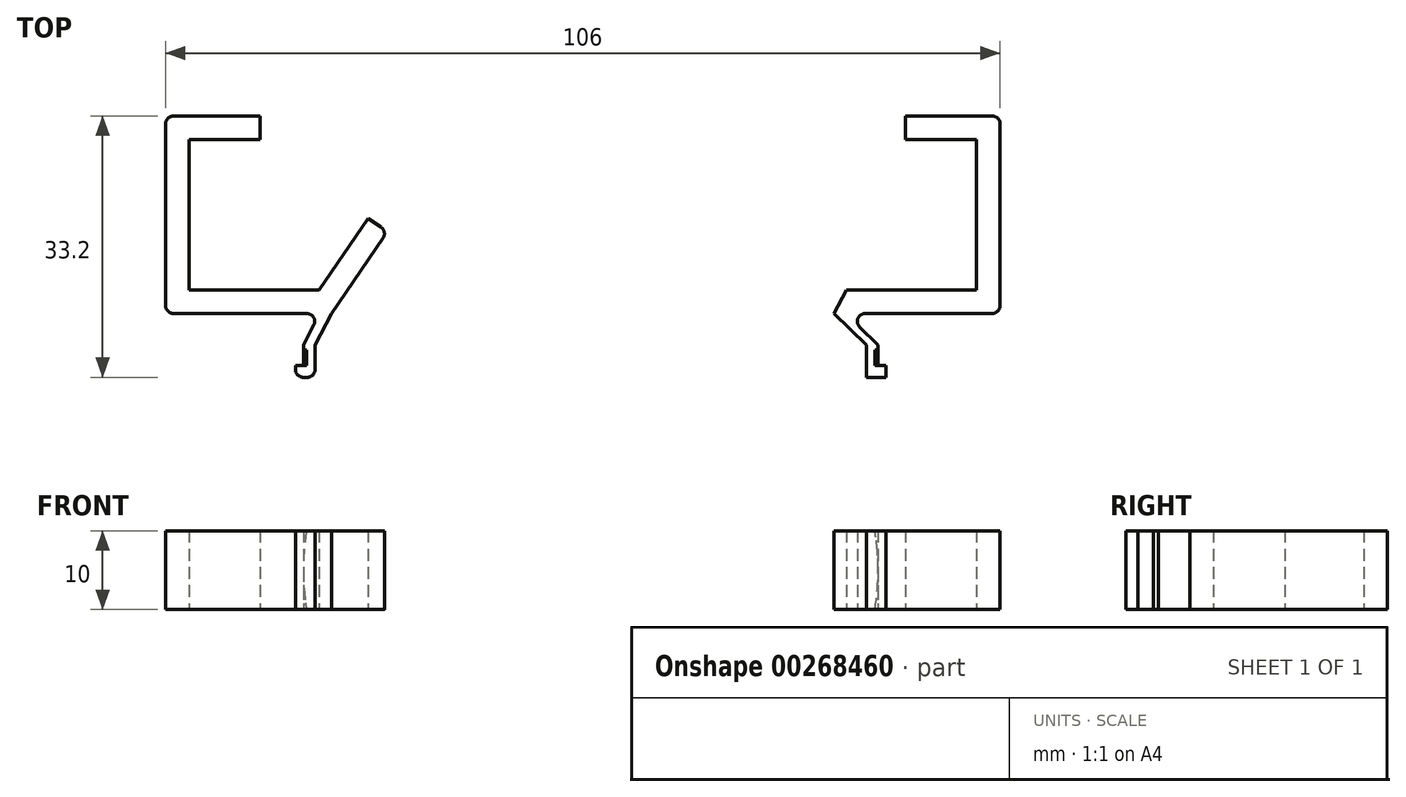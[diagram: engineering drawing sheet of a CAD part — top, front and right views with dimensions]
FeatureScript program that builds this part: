
annotation { "Feature Type Name" : "Feature", "Feature Type Description" : "" }
export const myFeature = defineFeature(function(context is Context, id is Id, definition is map)
    precondition{}
    {
        {
            var Q0;
            Q0=qCreatedBy(makeId("Top.planeOp"),FACE);
            var sketch = newSketch(context, id + "F0", { "sketchPlane" : qUnion([Q0])});
            skLineSegment(sketch, "E0", {"start": v(0, 0) * mm, "end": v(0, 19.1) * mm});
            skLineSegment(sketch, "E1", {"start": v(0, 19.1) * mm, "end": v(9, 19.1) * mm});
            skLineSegment(sketch, "E2", {"start": v(0, 0) * mm, "end": v(16.5, 0) * mm});
            skLineSegment(sketch, "E3", {"start": v(16.5, 0) * mm, "end": v(22.7, 9.1) * mm});
            skLineSegment(sketch, "E4.0", {"start": v(-3, 22.1) * mm, "end": v(9, 22.1) * mm});
            skLineSegment(sketch, "E4.1", {"start": v(-3, -3) * mm, "end": v(-3, 22.1) * mm});
            skLineSegment(sketch, "E4.2", {"start": v(-3, -3) * mm, "end": v(18.09, -3) * mm});
            skLineSegment(sketch, "E4.3", {"start": v(18.09, -3) * mm, "end": v(25.18, 7.41) * mm});
            skLineSegment(sketch, "E5", {"start": v(9, 22.1) * mm, "end": v(9, 19.1) * mm});
            skLineSegment(sketch, "E6", {"start": v(22.7, 9.1) * mm, "end": v(25.18, 7.41) * mm});
            skLineSegment(sketch, "E7", {"start": v(50, 52.55) * mm, "end": v(50, -36.88) * mm, "construction": true});
            skLineSegment(sketch, "E8.MirrorCS", {"start": v(91, 22.1) * mm, "end": v(91, 19.1) * mm});
            skLineSegment(sketch, "E9.MirrorCS", {"start": v(103, -3) * mm, "end": v(103, 22.1) * mm});
            skLineSegment(sketch, "E10.MirrorCS", {"start": v(103, 22.1) * mm, "end": v(91, 22.1) * mm});
            skLineSegment(sketch, "E11.MirrorCS", {"start": v(100, 19.1) * mm, "end": v(91, 19.1) * mm});
            skLineSegment(sketch, "E12.MirrorCS", {"start": v(103, -3) * mm, "end": v(81.91, -3) * mm});
            skLineSegment(sketch, "E13.MirrorCS", {"start": v(100, 0) * mm, "end": v(83.5, 0) * mm});
            skLineSegment(sketch, "E14.MirrorCS", {"start": v(100, 0) * mm, "end": v(100, 19.1) * mm});
            skLineSegment(sketch, "E15.bottom", {"start": v(10.1, -7) * mm, "end": v(14.5, -7) * mm, "construction": true});
            skLineSegment(sketch, "E15.top", {"start": v(10.1, -9.6) * mm, "end": v(14.5, -9.6) * mm});
            skLineSegment(sketch, "E15.left", {"start": v(10.1, -7) * mm, "end": v(10.1, -9.6) * mm, "construction": true});
            skLineSegment(sketch, "E15.right", {"start": v(14.5, -7) * mm, "end": v(14.5, -9.6) * mm});
            skLineSegment(sketch, "E16.0", {"start": v(13.5, -11.1) * mm, "end": v(16, -11.1) * mm});
            skLineSegment(sketch, "E16.1", {"start": v(16, -7) * mm, "end": v(16, -11.1) * mm});
            skLineSegment(sketch, "E17", {"start": v(13.5, -9.6) * mm, "end": v(13.5, -11.1) * mm});
            skLineSegment(sketch, "E18", {"start": v(81.91, -3) * mm, "end": v(86, -7) * mm});
            skLineSegment(sketch, "E19", {"start": v(87.5, -7) * mm, "end": v(83.41, -3) * mm});
            skLineSegment(sketch, "E20", {"start": v(81.91, -3) * mm, "end": v(83.5, 0) * mm});
            skLineSegment(sketch, "E21", {"start": v(87.5, -7) * mm, "end": v(87.5, -9.6) * mm});
            skLineSegment(sketch, "E22", {"start": v(87.5, -9.6) * mm, "end": v(88.5, -9.6) * mm});
            skLineSegment(sketch, "E23", {"start": v(88.5, -9.6) * mm, "end": v(88.5, -11.1) * mm});
            skLineSegment(sketch, "E24", {"start": v(88.5, -11.1) * mm, "end": v(86, -11.1) * mm});
            skLineSegment(sketch, "E25", {"start": v(86, -11.1) * mm, "end": v(86, -7) * mm});
            skLineSegment(sketch, "E26", {"start": v(14.5, -7) * mm, "end": v(16.59, -3) * mm});
            skLineSegment(sketch, "E27", {"start": v(16, -7) * mm, "end": v(18.09, -3) * mm});
            skSolve(sketch);
        }
        {
            var Q0;
            Q0=makeQuery(id+"F0.imprint","IMPRINT",FACE,{"disambiguationData":[TD([[makeQuery(id+"F0.imprint","IMPRINT",EDGE,{"derivedFrom":sQuery(id+"F0.wireOp",EDGE,"E8.MirrorCS")}),1.0]])]});
            var Q1;
            {var subQ2=sQuery(id+"F0.wireOp",EDGE,"7fd3f9bc-cb2d-437e-a477-eb83bc3e467c0.MirrorCS");Q1=makeQuery(id+"F0.imprint","IMPRINT",FACE,{"disambiguationData":[TD([[makeQuery(id+"F0.imprint","IMPRINT",EDGE,{"derivedFrom":subQ2}),1.0]])]});}
            var Q2;
            Q2=makeQuery(id+"F0.imprint","IMPRINT",FACE,{"disambiguationData":[TD([[makeQuery(id+"F0.imprint","IMPRINT",EDGE,{"derivedFrom":sQuery(id+"F0.wireOp",EDGE,"E0")}),1.0]])]});
            var Q3;
            {var subQ1=sQuery(id+"F0.wireOp",EDGE,"E15.right");Q3=makeQuery(id+"F0.imprint","IMPRINT",FACE,{"disambiguationData":[TD([[makeQuery(id+"F0.imprint","IMPRINT",EDGE,{"derivedFrom":subQ1}),1.0]])]});}
            var Q4;
            {var subQ0=sQuery(id+"F0.wireOp",EDGE,"E18");Q4=makeQuery(id+"F0.imprint","IMPRINT",FACE,{"disambiguationData":[TD([[makeQuery(id+"F0.imprint","IMPRINT",EDGE,{"derivedFrom":subQ0}),1.0]])]});}
            extrude(context, id + "F1", {"entities" : qUnion([Q0, Q1, Q2, Q3, Q4]), "depth" : 10 * mm, "offsetDistance" : 25 * mm, "symmetric" : true});
        }
        {
            var Q0;
            Q0=makeQuery(id+"F1.opExtrude","SWEPT_FACE",FACE,{"disambiguationData":[OSD([sQuery(id+"F0.wireOp",EDGE,"E15.top")])]});
            var sketch = newSketch(context, id + "F2", { "sketchPlane" : qUnion([Q0])});
            skPoint(sketch, "E28.0", {"position": v(-87.5, 0) * mm});
            skPoint(sketch, "E29.0", {"position": v(-14.5, 0) * mm});
            skLineSegment(sketch, "E30", {"start": v(-87.5, 0) * mm, "end": v(-14.5, 0) * mm, "construction": true});
            skLineSegment(sketch, "E31", {"start": v(-51, 0) * mm, "end": v(-51, 14.66) * mm, "construction": true});
            skCircle(sketch, "E32", {"center": v(-51, 0) * mm, "radius": 36.5 * mm});
            skCircle(sketch, "E33", {"center": v(-51, 0) * mm, "radius": 39.5 * mm});
            skSolve(sketch);
        }
        {
            var Q0;
            Q0=makeQuery(id+"F1.opExtrude","SWEPT_EDGE",EDGE,{"disambiguationData":[OSD([sQuery(id+"F0.wireOp",EDGE,"E9.MirrorCS"),sQuery(id+"F0.wireOp",EDGE,"E10.MirrorCS")])]});
            var Q1;
            Q1=makeQuery(id+"F1.opExtrude","SWEPT_EDGE",EDGE,{"disambiguationData":[OSD([sQuery(id+"F0.wireOp",EDGE,"E9.MirrorCS"),sQuery(id+"F0.wireOp",EDGE,"E12.MirrorCS")])]});
            var Q2;
            Q2=makeQuery(id+"F1.opExtrude","SWEPT_EDGE",EDGE,{"disambiguationData":[OSD([sQuery(id+"F0.wireOp",EDGE,"5a6db4d1-ee95-410c-8e2b-245da783c4610.MirrorCS"),sQuery(id+"F0.wireOp",EDGE,"12efcd92-a749-4238-9ad8-4c92c0031cb60.MirrorCS")])]});
            var Q3;
            Q3=makeQuery(id+"F1.opExtrude","SWEPT_EDGE",EDGE,{"disambiguationData":[OSD([sQuery(id+"F0.wireOp",EDGE,"12efcd92-a749-4238-9ad8-4c92c0031cb60.MirrorCS"),sQuery(id+"F0.wireOp",EDGE,"af5a5f1a-a19b-42ac-9b84-1e42bc72fd6b0.MirrorCS")])]});
            var Q4;
            Q4=makeQuery(id+"F1.opExtrude","SWEPT_EDGE",EDGE,{"disambiguationData":[OSD([sQuery(id+"F0.wireOp",EDGE,"fc325f98-27ae-4ef3-95bf-a05a649279151.MirrorCS"),sQuery(id+"F0.wireOp",EDGE,"fc325f98-27ae-4ef3-95bf-a05a649279157.MirrorCS")])]});
            var Q5;
            Q5=makeQuery(id+"F1.opExtrude","SWEPT_EDGE",EDGE,{"disambiguationData":[OSD([sQuery(id+"F0.wireOp",EDGE,"E16.0"),sQuery(id+"F0.wireOp",EDGE,"E17")])]});
            var Q6;
            Q6=makeQuery(id+"F1.opExtrude","SWEPT_EDGE",EDGE,{"disambiguationData":[OSD([sQuery(id+"F0.wireOp",EDGE,"E16.0"),sQuery(id+"F0.wireOp",EDGE,"E16.1")])]});
            var Q7;
            Q7=makeQuery(id+"F1.opExtrude","SWEPT_EDGE",EDGE,{"disambiguationData":[OSD([sQuery(id+"F0.wireOp",EDGE,"E4.3"),sQuery(id+"F0.wireOp",EDGE,"E6")])]});
            var Q8;
            Q8=makeQuery(id+"F1.opExtrude","SWEPT_EDGE",EDGE,{"disambiguationData":[OSD([sQuery(id+"F0.wireOp",EDGE,"E4.1"),sQuery(id+"F0.wireOp",EDGE,"E4.2")])]});
            var Q9;
            Q9=makeQuery(id+"F1.opExtrude","SWEPT_EDGE",EDGE,{"disambiguationData":[OSD([sQuery(id+"F0.wireOp",EDGE,"E4.0"),sQuery(id+"F0.wireOp",EDGE,"E4.1")])]});
            fillet(context, id + "F3", {"entities" : qUnion([Q0, Q1, Q2, Q3, Q4, Q5, Q6, Q7, Q8, Q9]), "radius" : 1 * mm, "tangentPropagation" : true, "allowEdgeOverflow" : false});
        }
        {
            var Q0;
            Q0=makeQuery(id+"F1.opExtrude","SWEPT_EDGE",EDGE,{"disambiguationData":[OSD([sQuery(id+"F0.wireOp",EDGE,"E12.MirrorCS"),sQuery(id+"F0.wireOp",EDGE,"E19")])]});
            var Q1;
            Q1=makeQuery(id+"F1.opExtrude","SWEPT_EDGE",EDGE,{"disambiguationData":[OSD([sQuery(id+"F0.wireOp",EDGE,"E4.2"),sQuery(id+"F0.wireOp",EDGE,"E26")])]});
            fillet(context, id + "F4", {"entities" : qUnion([Q0, Q1]), "tangentPropagation" : true, "radius" : 1 * mm, "defaultsChanged" : false, "vertexSettings" : [], "allowEdgeOverflow" : false});
        }
        {
            var Q0;
            {var subQ0=sQuery(id+"F0.wireOp",EDGE,"E15.top");var subQ1=makeQuery(id+"F1.opExtrude","CAP_EDGE",EDGE,{"disambiguationData":[OSD([subQ0])],"isStart":true});Q0=makeQuery(id+"F2.imprint","IMPRINT",FACE,{"disambiguationData":[TD([[makeQuery(id+"F2.imprint","IMPRINT",EDGE,{"derivedFrom":subQ1}),-1.0]])]});}
            var sketch = newSketch(context, id + "F5", { "sketchPlane" : qUnion([Q0])});
            skPoint(sketch, "E34.0", {"position": v(-14.5, 0) * mm});
            skPoint(sketch, "E35.0", {"position": v(-14.5, 5) * mm});
            skPoint(sketch, "E36.0", {"position": v(-14.5, -5) * mm});
            skArc(sketch, "E37", {"start": v(-14.9, -5) * mm, "mid": v(-14.5, 0) * mm, "end": v(-14.9, 5) * mm});
            skLineSegment(sketch, "E38", {"start": v(-14.9, -5) * mm, "end": v(-14.5, -5) * mm});
            skLineSegment(sketch, "E39", {"start": v(-14.5, 0) * mm, "end": v(-14.5, -5) * mm});
            skLineSegment(sketch, "E40", {"start": v(-14.5, 0) * mm, "end": v(-14.5, 5) * mm});
            skLineSegment(sketch, "E41", {"start": v(-14.5, 5) * mm, "end": v(-14.9, 5) * mm});
            skSolve(sketch);
        }
        {
            var Q0;
            {var subQ0=sQuery(id+"F5.wireOp",EDGE,"E40");Q0=makeQuery(id+"F5.imprint","IMPRINT",FACE,{"disambiguationData":[TD([[makeQuery(id+"F5.imprint","IMPRINT",EDGE,{"derivedFrom":subQ0}),-1.0]])]});}
            var Q1;
            {var subQ2=sQuery(id+"F5.wireOp",EDGE,"E38");Q1=makeQuery(id+"F5.imprint","IMPRINT",FACE,{"disambiguationData":[TD([[makeQuery(id+"F5.imprint","IMPRINT",EDGE,{"derivedFrom":subQ2}),1.0]])]});}
            extrude(context, id + "F6", {"entities" : qUnion([Q0, Q1]), "operationType" : NewBodyOperationType.REMOVE, "depth" : 2 * mm, "offsetDistance" : 25 * mm});
        }
        {
            var Q0;
            Q0=makeQuery(id+"F1.opExtrude","SWEPT_FACE",FACE,{"disambiguationData":[OSD([sQuery(id+"F0.wireOp",EDGE,"E22")])]});
            var sketch = newSketch(context, id + "F7", { "sketchPlane" : qUnion([Q0])});
            skPoint(sketch, "E42.0", {"position": v(-87.5, 0) * mm});
            skPoint(sketch, "E43.0", {"position": v(-87.5, 5) * mm});
            skPoint(sketch, "E44.0", {"position": v(-87.5, -5) * mm});
            skArc(sketch, "E45", {"start": v(-87.1, 5) * mm, "mid": v(-87.5, 0) * mm, "end": v(-87.1, -5) * mm});
            skLineSegment(sketch, "E46", {"start": v(-87.1, 5) * mm, "end": v(-87.5, 5) * mm});
            skLineSegment(sketch, "E47", {"start": v(-87.5, 0) * mm, "end": v(-87.5, 5) * mm});
            skLineSegment(sketch, "E48", {"start": v(-87.5, 0) * mm, "end": v(-87.5, -5) * mm});
            skLineSegment(sketch, "E49", {"start": v(-87.5, -5) * mm, "end": v(-87.1, -5) * mm});
            skSolve(sketch);
        }
        {
            var Q0;
            {var subQ0=sQuery(id+"F7.wireOp",EDGE,"E46");Q0=makeQuery(id+"F7.imprint","IMPRINT",FACE,{"disambiguationData":[TD([[makeQuery(id+"F7.imprint","IMPRINT",EDGE,{"derivedFrom":subQ0}),1.0]])]});}
            var Q1;
            {var subQ2=sQuery(id+"F7.wireOp",EDGE,"E48");Q1=makeQuery(id+"F7.imprint","IMPRINT",FACE,{"disambiguationData":[TD([[makeQuery(id+"F7.imprint","IMPRINT",EDGE,{"derivedFrom":subQ2}),1.0]])]});}
            extrude(context, id + "F8", {"entities" : qUnion([Q0, Q1]), "operationType" : NewBodyOperationType.REMOVE, "depth" : 2 * mm, "offsetDistance" : 25 * mm});
        }
    });
